# Revit family: QF_COMENDA_6B0000_6B0000DD_6B0000DDPS_6B0002_6B0002DD_6B0002DDPS_CAT
name_source: partatom
category: Attrezzature speciali
units: mm (PartAtom-declared; Revit-internal decimal feet)

## family parameters
Basato su piano di lavoro = No
Condiviso = No
Numero OmniClass = 23.40.40.14
Punto di calcolo locali = No
Quota connettore circolare = Usa diametro
Sempre verticale = Sì
Taglio con vuoti quando caricato = No
Tipo di parte = Normale
Titolo OmniClass = Food Service Equipment

## types (6) — shared parameters
Altezza = 613 mm  [stored 2.01115 ft]
Altezza allacciamento acqua fredda da pavimento finito = 36 mm  [stored 0.11811 ft]
Altezza allacciamento elettrico da pavimento finito = 47 mm  [stored 0.154199 ft]
Altezza dello scarico diretto acqua da pavimento finito = 36 mm  [stored 0.11811 ft]
Corrente di funzionamento normale = 12 A
Diametro condotta acqua fredda = 1"
Diametro dello scarico diretto di acqua = 1 1/2"
Fase = 3
Frequenza = 50 Hz
Lunghezza = 460 mm  [stored 1.50919 ft]
Numero dei poli = 1
Peso netto = 36.00 kg
Pessione minima acqua fredda = 2000.0 Pa
Potenza elettrica = 2660 W
Produttore = COMENDA
Profondità = 521 mm  [stored 1.70932 ft]
Protezione contro le sovracorrenti = 16 A
Temperatura raccomandata per acqua fredda = 15 °C
Tensione = 230 V
URL = www.comenda.eu
zero-valued in all types: Prospetto di default

## per-type parameters (varying)
| type | Descrizione | Modello | URL catalogo |
| 6B0000 | SINGLE-PHASE GLASSWASHER | PB24 | https://www.comenda.eu |
| 6B0002 | SINGLE-PHASE GLASSWASHER WITH WATER SOFTENER | PB24 A | https://www.comenda.eu |
| 6B0000DDPS | SINGLE-PHASE GLASSWASHER WITH DRAIN PUMP, DETERGENT DOSING PUMP | PB24+ | https://comenda.eu |
| 6B0002DDPS | SINGLE-PHASE GLASSWASHER WITH WATER SOFTENER, DRAIN PUMP, DETERGENT DOSING PUMP | PB24 A+ | https://comenda.eu |
| 6B0000DD | SINGLE-PHASE GLASSWASHER | PB24 DD | https://comenda.eu |
| 6B0002DD | SINGLE-PHASE GLASSWASHER WITH WATER SOFTENER | PB24 A DD | https://comenda.eu |

note: [stored X ft] marks values corroborated as IEEE doubles in the binary element streams (Revit-internal decimal feet)

## geometry (parser evidence)
native form markers: Sweep x3
no freeform markers — native parametric forms only
